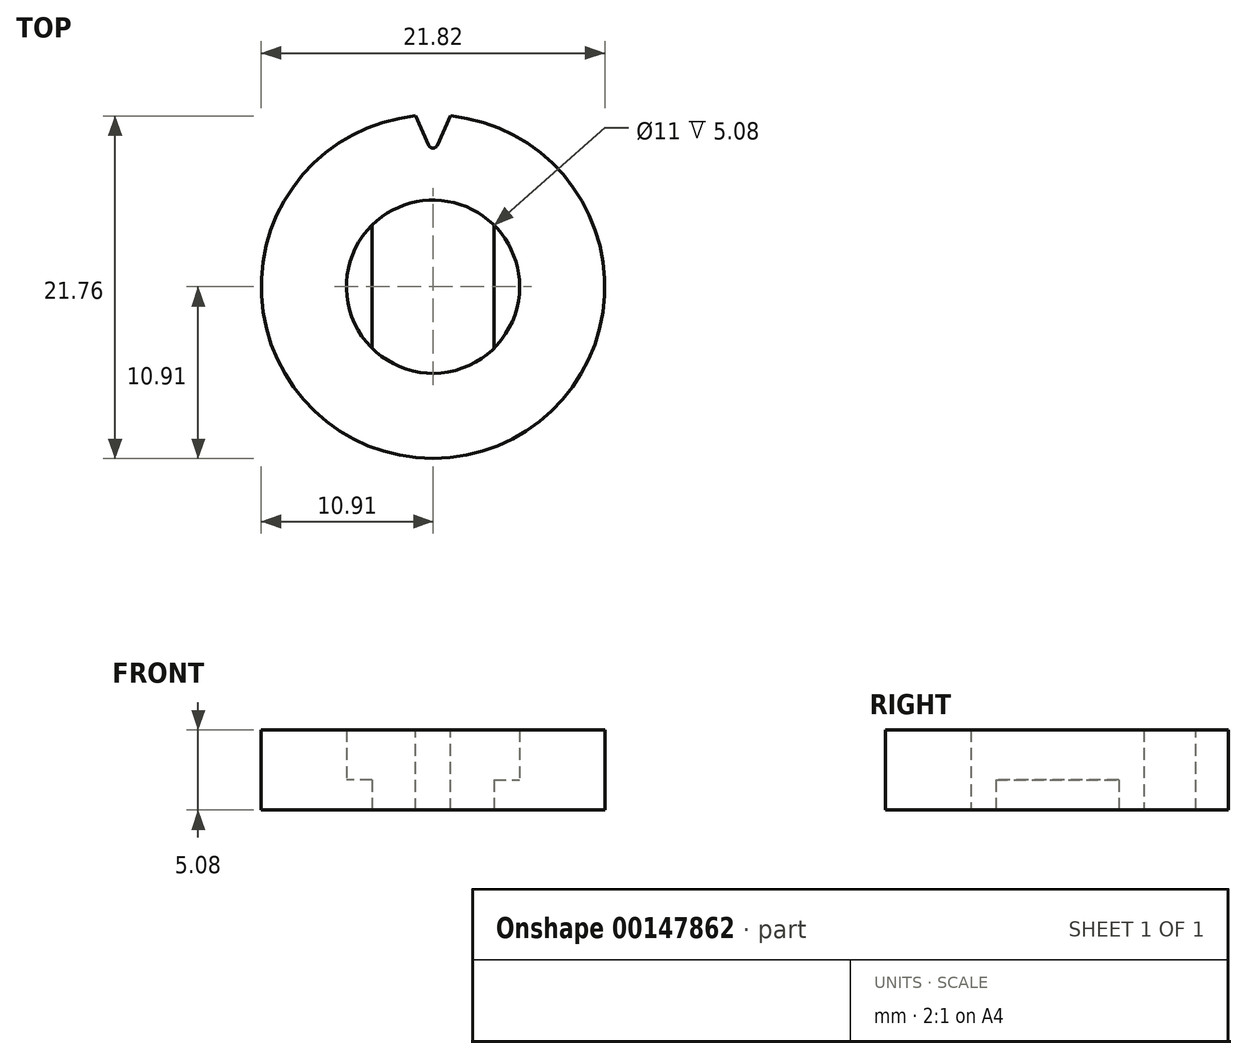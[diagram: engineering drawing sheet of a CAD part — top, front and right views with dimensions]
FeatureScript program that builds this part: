
annotation { "Feature Type Name" : "Feature", "Feature Type Description" : "" }
export const myFeature = defineFeature(function(context is Context, id is Id, definition is map)
    precondition{}
    {
        {
            var Q0;
            Q0=qCreatedBy(makeId("Top.planeOp"),FACE);
            var sketch = newSketch(context, id + "F0", { "sketchPlane" : qUnion([Q0])});
            skLineSegment(sketch, "E0.bottom", {"start": v(-3.87, -3.9) * mm, "end": v(3.87, -3.9) * mm, "construction": true});
            skLineSegment(sketch, "E0.top", {"start": v(-3.87, 3.9) * mm, "end": v(3.87, 3.9) * mm, "construction": true});
            skLineSegment(sketch, "E0.left", {"start": v(-3.87, -3.9) * mm, "end": v(-3.87, 3.9) * mm});
            skLineSegment(sketch, "E0.right", {"start": v(3.87, -3.9) * mm, "end": v(3.87, 3.9) * mm});
            skPoint(sketch, "E0.middle", {"position": v(0, 0) * mm});
            skArc(sketch, "E1", {"start": v(3.87, 3.9) * mm, "mid": v(0, 5.5) * mm, "end": v(-3.87, 3.9) * mm});
            skArc(sketch, "E2", {"start": v(-3.87, -3.9) * mm, "mid": v(0, -5.5) * mm, "end": v(3.87, -3.9) * mm});
            skCircle(sketch, "E3", {"center": v(0, 0) * mm, "radius": 10.9 * mm});
            skSolve(sketch);
        }
        {
            var Q0;
            Q0=makeQuery(id+"F0.imprint","IMPRINT",FACE,{"disambiguationData":[TD([[makeQuery(id+"F0.imprint","IMPRINT",EDGE,{"derivedFrom":sQuery(id+"F0.wireOp",EDGE,"E0.left")}),1.0]])]});
            extrude(context, id + "F1", {"entities" : qUnion([Q0]), "depth" : 5.08 * mm});
        }
        {
            var Q0;
            Q0=makeQuery(id+"F1.opExtrude","CAP_FACE",FACE,{"disambiguationData":[OSD([sQuery(id+"F0.wireOp",EDGE,"E0.left"),sQuery(id+"F0.wireOp",EDGE,"E0.right"),sQuery(id+"F0.wireOp",EDGE,"E1"),sQuery(id+"F0.wireOp",EDGE,"E2"),sQuery(id+"F0.wireOp",EDGE,"E3")])],"isStart":false});
            var sketch = newSketch(context, id + "F2", { "sketchPlane" : qUnion([Q0])});
            skLineSegment(sketch, "E4", {"start": v(0, 0) * mm, "end": v(0, 10.9) * mm, "construction": true});
            skLineSegment(sketch, "E5", {"start": v(0, 0) * mm, "end": v(0.75, 10.88) * mm, "construction": true});
            skArc(sketch, "E6", {"start": v(1.1, 10.85) * mm, "mid": v(0, 10.9) * mm, "end": v(-1.1, 10.85) * mm});
            skLineSegment(sketch, "E7", {"start": v(-1.1, 10.85) * mm, "end": v(-0.27, 8.98) * mm});
            skLineSegment(sketch, "E8", {"start": v(1.1, 10.85) * mm, "end": v(0.27, 8.98) * mm});
            skPoint(sketch, "E9", {"position": v(0.69, 9.92) * mm});
            skArc(sketch, "E10", {"start": v(-0.27, 8.98) * mm, "mid": v(0, 8.8) * mm, "end": v(0.27, 8.98) * mm});
            skSolve(sketch);
        }
        {
            var Q0;
            Q0=qSketchRegion(id+"F2",true);
            var Q1;
            Q1=makeQuery(id+"F1.opExtrude","CAP_FACE",FACE,{"disambiguationData":[OSD([sQuery(id+"F0.wireOp",EDGE,"E0.left"),sQuery(id+"F0.wireOp",EDGE,"E0.right"),sQuery(id+"F0.wireOp",EDGE,"E1"),sQuery(id+"F0.wireOp",EDGE,"E2"),sQuery(id+"F0.wireOp",EDGE,"E3")])],"isStart":true});
            extrude(context, id + "F3", {"entities" : qUnion([Q0]), "operationType" : NewBodyOperationType.REMOVE, "endBound" : BoundingType.UP_TO_SURFACE, "oppositeDirection" : true, "endBoundEntityFace" : qUnion([Q1]), "depth" : 25.4 * mm});
        }
        {
            var Q0;
            Q0=makeQuery(id+"F1.opExtrude","CAP_FACE",FACE,{"disambiguationData":[OSD([sQuery(id+"F0.wireOp",EDGE,"E0.left"),sQuery(id+"F0.wireOp",EDGE,"E0.right"),sQuery(id+"F0.wireOp",EDGE,"E1"),sQuery(id+"F0.wireOp",EDGE,"E2"),sQuery(id+"F0.wireOp",EDGE,"E3")])],"isStart":false});
            var sketch = newSketch(context, id + "F4", { "sketchPlane" : qUnion([Q0])});
            skCircle(sketch, "E11", {"center": v(0, 0) * mm, "radius": 5.5 * mm});
            skSolve(sketch);
        }
        {
            var Q0;
            Q0=qSketchRegion(id+"F4",true);
            extrude(context, id + "F5", {"entities" : qUnion([Q0]), "operationType" : NewBodyOperationType.REMOVE, "oppositeDirection" : true, "depth" : 3.17 * mm});
        }
    });
